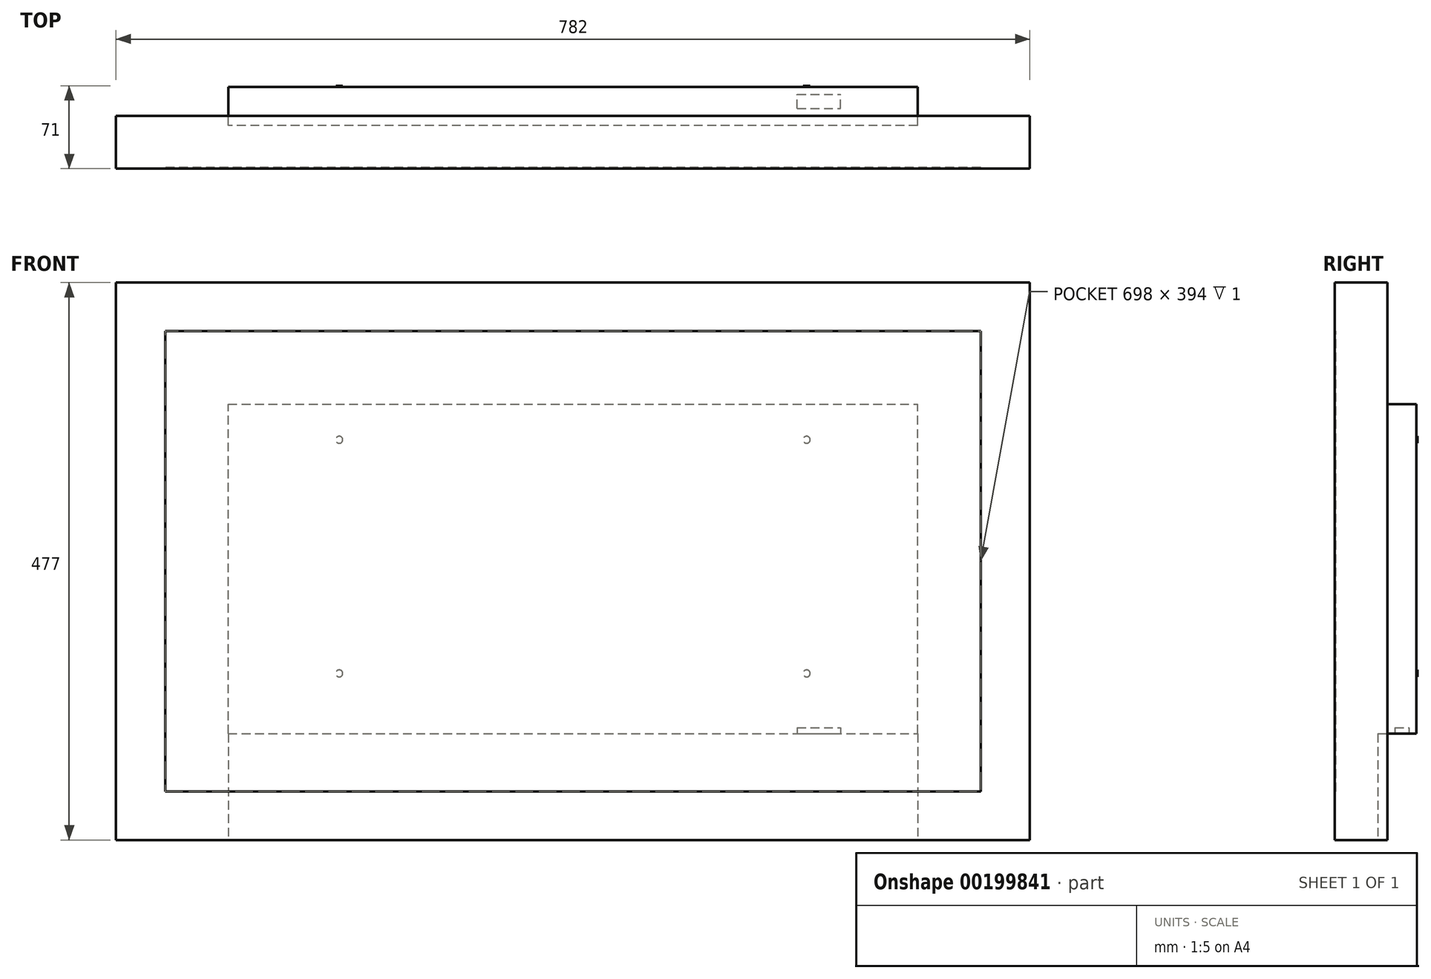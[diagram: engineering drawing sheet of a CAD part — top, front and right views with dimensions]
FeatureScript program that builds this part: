
annotation { "Feature Type Name" : "Feature", "Feature Type Description" : "" }
export const myFeature = defineFeature(function(context is Context, id is Id, definition is map)
    precondition{}
    {
        {
            var Q0;
            Q0=qCreatedBy(makeId("Front.planeOp"),FACE);
            var sketch = newSketch(context, id + "F0", { "sketchPlane" : qUnion([Q0])});
            skLineSegment(sketch, "E0.bottom", {"start": v(391, -238.5) * mm, "end": v(-391, -238.5) * mm});
            skLineSegment(sketch, "E0.top", {"start": v(391, 238.5) * mm, "end": v(-391, 238.5) * mm});
            skLineSegment(sketch, "E0.left", {"start": v(391, -238.5) * mm, "end": v(391, 238.5) * mm});
            skLineSegment(sketch, "E0.right", {"start": v(-391, -238.5) * mm, "end": v(-391, 238.5) * mm});
            skPoint(sketch, "E0.middle", {"position": v(0, 0) * mm});
            skSolve(sketch);
        }
        {
            var Q0;
            Q0=qSketchRegion(id+"F0",true);
            extrude(context, id + "F1", {"entities" : qUnion([Q0]), "depth" : 45 * mm});
        }
        {
            var Q0;
            Q0=makeQuery(id+"F1.opExtrude","CAP_FACE",FACE,{"disambiguationData":[OSD([sQuery(id+"F0.wireOp",EDGE,"E0.bottom"),sQuery(id+"F0.wireOp",EDGE,"E0.top"),sQuery(id+"F0.wireOp",EDGE,"E0.left"),sQuery(id+"F0.wireOp",EDGE,"E0.right")])],"isStart":true});
            var sketch = newSketch(context, id + "F2", { "sketchPlane" : qUnion([Q0])});
            skPoint(sketch, "E1.middle", {"position": v(0, 0) * mm});
            skLineSegment(sketch, "E2", {"start": v(0, 238.5) * mm, "end": v(0, -238.5) * mm, "construction": true});
            skLineSegment(sketch, "E3.bottom", {"start": v(295, -147.5) * mm, "end": v(-295, -147.5) * mm});
            skLineSegment(sketch, "E3.top", {"start": v(295, 134.5) * mm, "end": v(-295, 134.5) * mm});
            skLineSegment(sketch, "E3.left", {"start": v(295, -147.5) * mm, "end": v(295, 134.5) * mm});
            skLineSegment(sketch, "E3.right", {"start": v(-295, -147.5) * mm, "end": v(-295, 134.5) * mm});
            skPoint(sketch, "E3.middle", {"position": v(0, -6.5) * mm});
            skSolve(sketch);
        }
        {
            var Q0;
            Q0=qSketchRegion(id+"F2",true);
            extrude(context, id + "F3", {"entities" : qUnion([Q0]), "operationType" : NewBodyOperationType.ADD, "depth" : 25 * mm});
        }
        {
            var Q0;
            Q0=makeQuery(id+"F3.opExtrude","SWEPT_FACE",FACE,{"disambiguationData":[OSD([sQuery(id+"F2.wireOp",EDGE,"E3.bottom")])]});
            var sketch = newSketch(context, id + "F4", { "sketchPlane" : qUnion([Q0])});
            skLineSegment(sketch, "E4", {"start": v(295, -12.5) * mm, "end": v(-295, -12.5) * mm, "construction": true});
            skLineSegment(sketch, "E5.bottom", {"start": v(191.87, -6.53) * mm, "end": v(228.87, -6.53) * mm});
            skLineSegment(sketch, "E5.top", {"start": v(191.87, -18.47) * mm, "end": v(228.87, -18.47) * mm});
            skLineSegment(sketch, "E5.left", {"start": v(191.87, -6.53) * mm, "end": v(191.87, -18.47) * mm});
            skLineSegment(sketch, "E5.right", {"start": v(228.87, -6.53) * mm, "end": v(228.87, -18.47) * mm});
            skPoint(sketch, "E5.middle", {"position": v(210.37, -12.5) * mm});
            skSolve(sketch);
        }
        {
            var Q0;
            Q0=qSketchRegion(id+"F4",true);
            extrude(context, id + "F5", {"entities" : qUnion([Q0]), "operationType" : NewBodyOperationType.REMOVE, "oppositeDirection" : true, "depth" : 5 * mm});
        }
        {
            var Q0;
            Q0=makeQuery(id+"F1.opExtrude","CAP_FACE",FACE,{"disambiguationData":[OSD([sQuery(id+"F0.wireOp",EDGE,"E0.bottom"),sQuery(id+"F0.wireOp",EDGE,"E0.top"),sQuery(id+"F0.wireOp",EDGE,"E0.left"),sQuery(id+"F0.wireOp",EDGE,"E0.right")])],"isStart":false});
            var sketch = newSketch(context, id + "F6", { "sketchPlane" : qUnion([Q0])});
            skLineSegment(sketch, "E6.bottom", {"start": v(349, -197) * mm, "end": v(-349, -197) * mm});
            skLineSegment(sketch, "E6.top", {"start": v(349, 197) * mm, "end": v(-349, 197) * mm});
            skLineSegment(sketch, "E6.left", {"start": v(349, -197) * mm, "end": v(349, 197) * mm});
            skLineSegment(sketch, "E6.right", {"start": v(-349, -197) * mm, "end": v(-349, 197) * mm});
            skPoint(sketch, "E6.middle", {"position": v(0, 0) * mm});
            skSolve(sketch);
        }
        {
            var Q0;
            Q0=qSketchRegion(id+"F6",true);
            extrude(context, id + "F7", {"entities" : qUnion([Q0]), "operationType" : NewBodyOperationType.REMOVE, "oppositeDirection" : true, "depth" : 1 * mm});
        }
        {
            var Q0;
            Q0=makeQuery(id+"F1.opExtrude","CAP_FACE",FACE,{"disambiguationData":[OSD([sQuery(id+"F0.wireOp",EDGE,"E0.bottom"),sQuery(id+"F0.wireOp",EDGE,"E0.top"),sQuery(id+"F0.wireOp",EDGE,"E0.left"),sQuery(id+"F0.wireOp",EDGE,"E0.right")])],"isStart":true});
            var sketch = newSketch(context, id + "F8", { "sketchPlane" : qUnion([Q0])});
            skLineSegment(sketch, "E7.bottom", {"start": v(-295, -147.5) * mm, "end": v(295, -147.5) * mm});
            skLineSegment(sketch, "E7.top", {"start": v(-295, -238.5) * mm, "end": v(295, -238.5) * mm});
            skLineSegment(sketch, "E7.left", {"start": v(-295, -147.5) * mm, "end": v(-295, -238.5) * mm});
            skLineSegment(sketch, "E7.right", {"start": v(295, -147.5) * mm, "end": v(295, -238.5) * mm});
            skSolve(sketch);
        }
        {
            var Q0;
            Q0=qSketchRegion(id+"F8",true);
            extrude(context, id + "F9", {"entities" : qUnion([Q0]), "operationType" : NewBodyOperationType.REMOVE, "oppositeDirection" : true, "depth" : 8 * mm});
        }
        {
            var Q0;
            Q0=makeQuery(id+"F1.opExtrude","CAP_FACE",FACE,{"disambiguationData":[OSD([sQuery(id+"F0.wireOp",EDGE,"E0.bottom"),sQuery(id+"F0.wireOp",EDGE,"E0.top"),sQuery(id+"F0.wireOp",EDGE,"E0.left"),sQuery(id+"F0.wireOp",EDGE,"E0.right")])],"isStart":true});
            var sketch = newSketch(context, id + "F10", { "sketchPlane" : qUnion([Q0])});
            skLineSegment(sketch, "E8", {"start": v(0, 134.5) * mm, "end": v(0, -147.5) * mm, "construction": true});
            skCircle(sketch, "E9", {"center": v(-200, 104) * mm, "radius": 3 * mm});
            skLineSegment(sketch, "E10", {"start": v(-247.61, 4) * mm, "end": v(192.29, 4) * mm, "construction": true});
            skCircle(sketch, "E11.MirrorC", {"center": v(-200, -96) * mm, "radius": 3 * mm});
            skCircle(sketch, "E12.MirrorC", {"center": v(200, 104) * mm, "radius": 3 * mm});
            skCircle(sketch, "E13.MirrorC", {"center": v(200, -96) * mm, "radius": 3 * mm});
            skLineSegment(sketch, "E14", {"start": v(-391, 0) * mm, "end": v(391, 0) * mm, "construction": true});
            skSolve(sketch);
        }
        {
            var Q0;
            Q0=qSketchRegion(id+"F10",true);
            extrude(context, id + "F11", {"entities" : qUnion([Q0]), "operationType" : NewBodyOperationType.ADD, "depth" : 26 * mm});
        }
    });
